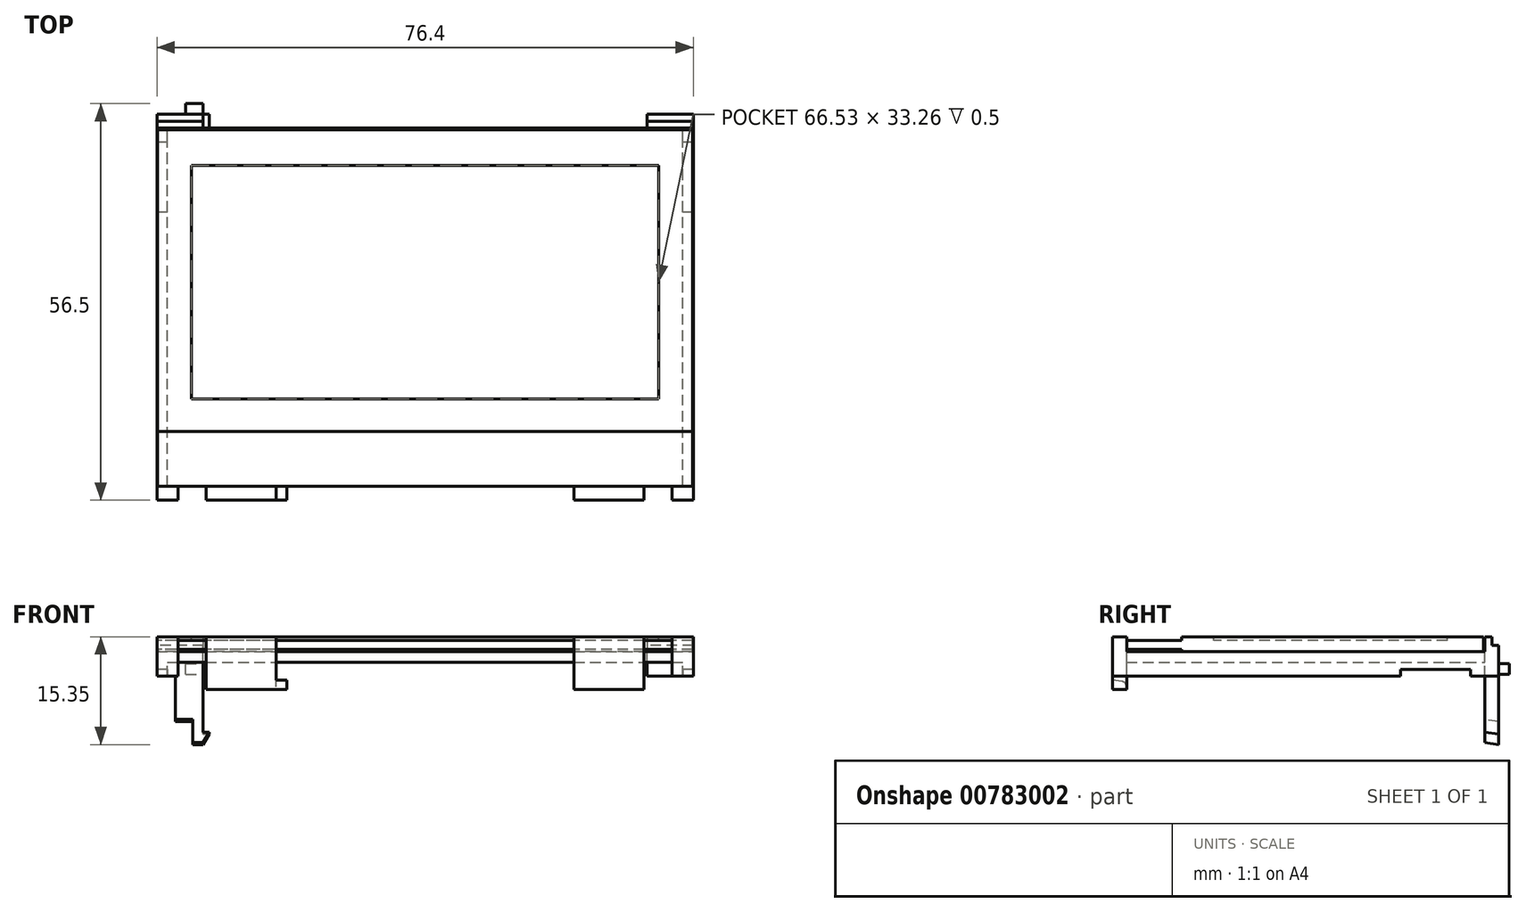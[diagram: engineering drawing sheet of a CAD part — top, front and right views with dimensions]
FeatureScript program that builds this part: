
annotation { "Feature Type Name" : "Feature", "Feature Type Description" : "" }
export const myFeature = defineFeature(function(context is Context, id is Id, definition is map)
    precondition{}
    {
        {
            var Q0;
            Q0=qCreatedBy(makeId("Top.planeOp"),FACE);
            var sketch = newSketch(context, id + "F0", { "sketchPlane" : qUnion([Q0])});
            skLineSegment(sketch, "E0.bottom", {"start": v(-38.2, 51) * mm, "end": v(38.2, 51) * mm});
            skLineSegment(sketch, "E0.top", {"start": v(-38.2, 0) * mm, "end": v(38.2, 0) * mm});
            skLineSegment(sketch, "E0.left", {"start": v(-38.2, 51) * mm, "end": v(-38.2, 0) * mm});
            skLineSegment(sketch, "E0.right", {"start": v(38.2, 51) * mm, "end": v(38.2, 0) * mm});
            skLineSegment(sketch, "E1", {"start": v(-38.2, 0) * mm, "end": v(-38.2, -2) * mm});
            skLineSegment(sketch, "E2", {"start": v(-38.2, -2) * mm, "end": v(-35.2, -2) * mm});
            skLineSegment(sketch, "E3", {"start": v(-35.2, -2) * mm, "end": v(-31.2, -2) * mm, "construction": true});
            skLineSegment(sketch, "E4", {"start": v(-31.2, -2) * mm, "end": v(-21.2, -2) * mm});
            skLineSegment(sketch, "E5", {"start": v(-21.2, -2) * mm, "end": v(-21.2, 0) * mm});
            skLineSegment(sketch, "E6", {"start": v(-35.2, -2) * mm, "end": v(-35.2, 0) * mm});
            skLineSegment(sketch, "E7", {"start": v(-31.2, -2) * mm, "end": v(-31.2, 0) * mm});
            skLineSegment(sketch, "E8", {"start": v(-38.2, 51) * mm, "end": v(-38.2, 53) * mm});
            skLineSegment(sketch, "E9", {"start": v(-38.2, 53) * mm, "end": v(-31.6, 53) * mm});
            skLineSegment(sketch, "E10", {"start": v(-31.6, 53) * mm, "end": v(-31.6, 51) * mm});
            skLineSegment(sketch, "E11", {"start": v(-36.7, 0) * mm, "end": v(-36.7, 51) * mm});
            skLineSegment(sketch, "E12", {"start": v(0, 0) * mm, "end": v(0, 51) * mm, "construction": true});
            skLineSegment(sketch, "E13.MirrorCS", {"start": v(31.6, 53) * mm, "end": v(31.6, 51) * mm});
            skLineSegment(sketch, "E14.MirrorCS", {"start": v(38.2, 53) * mm, "end": v(31.6, 53) * mm});
            skLineSegment(sketch, "E15.MirrorCS", {"start": v(38.2, 51) * mm, "end": v(38.2, 53) * mm});
            skLineSegment(sketch, "E16.MirrorCS", {"start": v(36.7, 0) * mm, "end": v(36.7, 51) * mm});
            skLineSegment(sketch, "E17.MirrorCS", {"start": v(38.2, 0) * mm, "end": v(38.2, -2) * mm});
            skLineSegment(sketch, "E18.MirrorCS", {"start": v(38.2, -2) * mm, "end": v(35.2, -2) * mm});
            skLineSegment(sketch, "E19.MirrorCS", {"start": v(35.2, -2) * mm, "end": v(35.2, 0) * mm});
            skLineSegment(sketch, "E20.MirrorCS", {"start": v(35.2, -2) * mm, "end": v(31.2, -2) * mm, "construction": true});
            skLineSegment(sketch, "E21.MirrorCS", {"start": v(31.2, -2) * mm, "end": v(31.2, 0) * mm});
            skLineSegment(sketch, "E22.MirrorCS", {"start": v(31.2, -2) * mm, "end": v(21.2, -2) * mm});
            skLineSegment(sketch, "E23.MirrorCS", {"start": v(21.2, -2) * mm, "end": v(21.2, 0) * mm});
            skLineSegment(sketch, "E24", {"start": v(-10, 0) * mm, "end": v(-10, -2) * mm});
            skLineSegment(sketch, "E25", {"start": v(-10, -2) * mm, "end": v(10, -2) * mm});
            skLineSegment(sketch, "E26", {"start": v(10, -2) * mm, "end": v(10, 0) * mm});
            skLineSegment(sketch, "E27", {"start": v(0, 0) * mm, "end": v(0, -2) * mm, "construction": true});
            skSolve(sketch);
        }
        {
            var Q0;
            {var subQ10=sQuery(id+"F0.wireOp",EDGE,"E11");Q0=makeQuery(id+"F0.imprint","IMPRINT",FACE,{"disambiguationData":[TD([[makeQuery(id+"F0.imprint","IMPRINT",EDGE,{"derivedFrom":subQ10}),-1.0]])]});}
            var Q1;
            {var subQ0=sQuery(id+"F0.wireOp",EDGE,"E0.left");Q1=makeQuery(id+"F0.imprint","IMPRINT",FACE,{"disambiguationData":[TD([[makeQuery(id+"F0.imprint","IMPRINT",EDGE,{"derivedFrom":subQ0}),1.0]])]});}
            var Q2;
            {var subQ0=sQuery(id+"F0.wireOp",EDGE,"E0.right");Q2=makeQuery(id+"F0.imprint","IMPRINT",FACE,{"disambiguationData":[TD([[makeQuery(id+"F0.imprint","IMPRINT",EDGE,{"derivedFrom":subQ0}),-1.0]])]});}
            extrude(context, id + "F1", {"entities" : qUnion([Q0, Q1, Q2]), "oppositeDirection" : true, "depth" : 1.5 * mm, "offsetDistance" : 25 * mm});
        }
        {
            var Q0;
            {var subQ3=sQuery(id+"F0.wireOp",EDGE,"E1");Q0=makeQuery(id+"F0.imprint","IMPRINT",FACE,{"disambiguationData":[TD([[makeQuery(id+"F0.imprint","IMPRINT",EDGE,{"derivedFrom":subQ3}),1.0]])]});}
            var Q1;
            {var subQ0=sQuery(id+"F0.wireOp",EDGE,"E17.MirrorCS");Q1=makeQuery(id+"F0.imprint","IMPRINT",FACE,{"disambiguationData":[TD([[makeQuery(id+"F0.imprint","IMPRINT",EDGE,{"derivedFrom":subQ0}),-1.0]])]});}
            var Q2;
            {var subQ0=sQuery(id+"F0.wireOp",EDGE,"E0.right");Q2=makeQuery(id+"F0.imprint","IMPRINT",FACE,{"disambiguationData":[TD([[makeQuery(id+"F0.imprint","IMPRINT",EDGE,{"derivedFrom":subQ0}),-1.0]])]});}
            var Q3;
            {var subQ0=sQuery(id+"F0.wireOp",EDGE,"E13.MirrorCS");Q3=makeQuery(id+"F0.imprint","IMPRINT",FACE,{"disambiguationData":[TD([[makeQuery(id+"F0.imprint","IMPRINT",EDGE,{"derivedFrom":subQ0}),1.0]])]});}
            var Q4;
            {var subQ3=sQuery(id+"F0.wireOp",EDGE,"E8");Q4=makeQuery(id+"F0.imprint","IMPRINT",FACE,{"disambiguationData":[TD([[makeQuery(id+"F0.imprint","IMPRINT",EDGE,{"derivedFrom":subQ3}),-1.0]])]});}
            var Q5;
            {var subQ0=sQuery(id+"F0.wireOp",EDGE,"E0.left");Q5=makeQuery(id+"F0.imprint","IMPRINT",FACE,{"disambiguationData":[TD([[makeQuery(id+"F0.imprint","IMPRINT",EDGE,{"derivedFrom":subQ0}),1.0]])]});}
            extrude(context, id + "F2", {"entities" : qUnion([Q0, Q1, Q2, Q3, Q4, Q5]), "operationType" : NewBodyOperationType.ADD, "oppositeDirection" : true, "depth" : 3.5 * mm, "offsetDistance" : 25 * mm});
        }
        {
            var Q0;
            Q0=makeQuery(id+"F0.imprint","IMPRINT",FACE,{"disambiguationData":[TD([[makeQuery(id+"F0.imprint","IMPRINT",EDGE,{"derivedFrom":sQuery(id+"F0.wireOp",EDGE,"E4")}),1.0]])]});
            var Q1;
            {var subQ0=sQuery(id+"F0.wireOp",EDGE,"E24");Q1=makeQuery(id+"F0.imprint","IMPRINT",FACE,{"disambiguationData":[TD([[makeQuery(id+"F0.imprint","IMPRINT",EDGE,{"derivedFrom":subQ0}),1.0]])]});}
            var Q2;
            {var subQ0=sQuery(id+"F0.wireOp",EDGE,"E21.MirrorCS");Q2=makeQuery(id+"F0.imprint","IMPRINT",FACE,{"disambiguationData":[TD([[makeQuery(id+"F0.imprint","IMPRINT",EDGE,{"derivedFrom":subQ0}),1.0]])]});}
            extrude(context, id + "F3", {"entities" : qUnion([Q0, Q1, Q2]), "operationType" : NewBodyOperationType.ADD, "oppositeDirection" : true, "depth" : 5.4 * mm, "offsetDistance" : 25 * mm});
        }
        {
            var Q0;
            {var subQ3=sQuery(id+"F0.wireOp",EDGE,"E8");Q0=makeQuery(id+"F0.imprint","IMPRINT",FACE,{"disambiguationData":[TD([[makeQuery(id+"F0.imprint","IMPRINT",EDGE,{"derivedFrom":subQ3}),-1.0]])]});}
            var Q1;
            {var subQ0=sQuery(id+"F0.wireOp",EDGE,"E13.MirrorCS");Q1=makeQuery(id+"F0.imprint","IMPRINT",FACE,{"disambiguationData":[TD([[makeQuery(id+"F0.imprint","IMPRINT",EDGE,{"derivedFrom":subQ0}),1.0]])]});}
            var Q2;
            {var subQ3=sQuery(id+"F0.wireOp",EDGE,"E1");Q2=makeQuery(id+"F0.imprint","IMPRINT",FACE,{"disambiguationData":[TD([[makeQuery(id+"F0.imprint","IMPRINT",EDGE,{"derivedFrom":subQ3}),1.0]])]});}
            var Q3;
            Q3=makeQuery(id+"F0.imprint","IMPRINT",FACE,{"disambiguationData":[TD([[makeQuery(id+"F0.imprint","IMPRINT",EDGE,{"derivedFrom":sQuery(id+"F0.wireOp",EDGE,"E4")}),1.0]])]});
            var Q4;
            {var subQ0=sQuery(id+"F0.wireOp",EDGE,"E21.MirrorCS");Q4=makeQuery(id+"F0.imprint","IMPRINT",FACE,{"disambiguationData":[TD([[makeQuery(id+"F0.imprint","IMPRINT",EDGE,{"derivedFrom":subQ0}),1.0]])]});}
            var Q5;
            {var subQ0=sQuery(id+"F0.wireOp",EDGE,"E17.MirrorCS");Q5=makeQuery(id+"F0.imprint","IMPRINT",FACE,{"disambiguationData":[TD([[makeQuery(id+"F0.imprint","IMPRINT",EDGE,{"derivedFrom":subQ0}),-1.0]])]});}
            var Q6;
            {var subQ0=sQuery(id+"F0.wireOp",EDGE,"E24");Q6=makeQuery(id+"F0.imprint","IMPRINT",FACE,{"disambiguationData":[TD([[makeQuery(id+"F0.imprint","IMPRINT",EDGE,{"derivedFrom":subQ0}),1.0]])]});}
            extrude(context, id + "F4", {"entities" : qUnion([Q0, Q1, Q2, Q3, Q4, Q5, Q6]), "operationType" : NewBodyOperationType.ADD, "depth" : 2.1 * mm, "offsetDistance" : 25 * mm});
        }
        {
            var Q0;
            Q0=makeQuery(id+"F1.opExtrude","CAP_FACE",FACE,{"disambiguationData":[OSD([sQuery(id+"F0.wireOp",EDGE,"E0.bottom"),sQuery(id+"F0.wireOp",EDGE,"E0.top"),sQuery(id+"F0.wireOp",EDGE,"E0.left"),sQuery(id+"F0.wireOp",EDGE,"E0.right")])],"isStart":false});
            var sketch = newSketch(context, id + "F5", { "sketchPlane" : qUnion([Q0])});
            skLineSegment(sketch, "E28.bottom", {"start": v(-36, 0) * mm, "end": v(36, 0) * mm});
            skLineSegment(sketch, "E28.top", {"start": v(-36, -30) * mm, "end": v(36, -30) * mm});
            skLineSegment(sketch, "E28.left", {"start": v(-36, 0) * mm, "end": v(-36, -30) * mm});
            skLineSegment(sketch, "E28.right", {"start": v(36, 0) * mm, "end": v(36, -30) * mm});
            skSolve(sketch);
        }
        {
            var Q0;
            Q0 = qSketchRegion(id + "F5", true);
            extrude(context, id + "F6", {"entities" : qUnion([Q0]), "operationType" : NewBodyOperationType.ADD, "depth" : 1 * mm, "offsetDistance" : 25 * mm});
        }
        {
            var Q0;
            Q0=qCreatedBy(makeId("Right.planeOp"),FACE);
            var sketch = newSketch(context, id + "F7", { "sketchPlane" : qUnion([Q0])});
            skLineSegment(sketch, "E29", {"start": v(50.8, 2.1) * mm, "end": v(50.8, 0) * mm});
            skLineSegment(sketch, "E30", {"start": v(50.8, 0) * mm, "end": v(7.8, 0) * mm});
            skLineSegment(sketch, "E31", {"start": v(7.8, 0) * mm, "end": v(7.8, 0.3) * mm});
            skLineSegment(sketch, "E32", {"start": v(7.8, 0.3) * mm, "end": v(7.8, 1.6) * mm});
            skLineSegment(sketch, "E33", {"start": v(7.8, 1.6) * mm, "end": v(7.8, 2.1) * mm});
            skLineSegment(sketch, "E34", {"start": v(7.8, 2.1) * mm, "end": v(50.8, 2.1) * mm});
            skLineSegment(sketch, "E35", {"start": v(7.8, 0.3) * mm, "end": v(0, 0.3) * mm});
            skLineSegment(sketch, "E36", {"start": v(0, 0.3) * mm, "end": v(0, 1.6) * mm});
            skLineSegment(sketch, "E37", {"start": v(0, 1.6) * mm, "end": v(7.8, 1.6) * mm});
            skLineSegment(sketch, "E38", {"start": v(7.8, 0) * mm, "end": v(0, 0) * mm, "construction": true});
            skLineSegment(sketch, "E39", {"start": v(0, 0) * mm, "end": v(0, 0.3) * mm, "construction": true});
            skSolve(sketch);
        }
        {
            var Q0;
            Q0 = qSketchRegion(id + "F7", true);
            extrude(context, id + "F8", {"entities" : qUnion([Q0]), "endBound" : BoundingType.SYMMETRIC, "depth" : 76.2 * mm, "offsetDistance" : 25 * mm});
        }
        {
            var Q0;
            Q0=makeQuery(id+"F8.opExtrude","SWEPT_FACE",FACE,{"disambiguationData":[OSD([sQuery(id+"F7.wireOp",EDGE,"E34")])]});
            var sketch = newSketch(context, id + "F9", { "sketchPlane" : qUnion([Q0])});
            skLineSegment(sketch, "E40.bottom", {"start": v(-33.26, 45.68) * mm, "end": v(33.26, 45.68) * mm});
            skLineSegment(sketch, "E40.top", {"start": v(-33.26, 12.42) * mm, "end": v(33.27, 12.42) * mm});
            skLineSegment(sketch, "E40.left", {"start": v(-33.27, 45.68) * mm, "end": v(-33.27, 12.42) * mm});
            skLineSegment(sketch, "E40.right", {"start": v(33.26, 45.68) * mm, "end": v(33.26, 12.42) * mm});
            skLineSegment(sketch, "E41", {"start": v(0, 50.8) * mm, "end": v(0, 45.68) * mm, "construction": true});
            skSolve(sketch);
        }
        {
            var Q0;
            Q0 = qSketchRegion(id + "F9", true);
            extrude(context, id + "F10", {"entities" : qUnion([Q0]), "operationType" : NewBodyOperationType.REMOVE, "oppositeDirection" : true, "depth" : 0.5 * mm, "offsetDistance" : 25 * mm});
        }
        {
            var Q0;
            {var subQ0=sQuery(id+"F0.wireOp",EDGE,"E5");Q0=makeQuery(id+"F4.boolean.opBoolean","MERGE",FACE,{"derivedFrom":[makeQuery(id+"F3.opExtrude","SWEPT_FACE",FACE,{"disambiguationData":[OSD([subQ0])]}),makeQuery(id+"F4.opExtrude","SWEPT_FACE",FACE,{"disambiguationData":[OSD([subQ0])]})]});}
            var sketch = newSketch(context, id + "F11", { "sketchPlane" : qUnion([Q0])});
            skLineSegment(sketch, "E42.0", {"start": v(-2, -5.4) * mm, "end": v(0, -5.4) * mm});
            skLineSegment(sketch, "E43", {"start": v(0, -5.4) * mm, "end": v(0, -4.32) * mm});
            skLineSegment(sketch, "E44", {"start": v(0, -4.32) * mm, "end": v(-2, -4.04) * mm});
            skLineSegment(sketch, "E45", {"start": v(-2, -4.04) * mm, "end": v(-2, -5.4) * mm});
            skPoint(sketch, "E46.0", {"position": v(0, -2.5) * mm});
            skLineSegment(sketch, "E47", {"start": v(-1, -4.18) * mm, "end": v(-0.75, -2.4) * mm, "construction": true});
            skLineSegment(sketch, "E48", {"start": v(-0.75, -2.4) * mm, "end": v(0, -2.5) * mm, "construction": true});
            skLineSegment(sketch, "E49.0", {"start": v(53, -3.5) * mm, "end": v(51, -3.5) * mm, "construction": true});
            skLineSegment(sketch, "E50", {"start": v(0, -2.5) * mm, "end": v(51, -9.67) * mm, "construction": true});
            skLineSegment(sketch, "E51", {"start": v(53, -3.5) * mm, "end": v(53, -9.95) * mm, "construction": true});
            skLineSegment(sketch, "E52", {"start": v(53, -9.95) * mm, "end": v(51, -9.67) * mm});
            skLineSegment(sketch, "E53", {"start": v(51, -3.5) * mm, "end": v(51, -9.67) * mm, "construction": true});
            skPoint(sketch, "E54.0", {"position": v(0, -5.4) * mm});
            skPoint(sketch, "E54.1", {"position": v(-2, -5.4) * mm});
            skSolve(sketch);
        }
        {
            var Q0;
            Q0 = qSketchRegion(id + "F11", true);
            extrude(context, id + "F12", {"entities" : qUnion([Q0]), "operationType" : NewBodyOperationType.ADD, "depth" : 1.5 * mm, "offsetDistance" : 25 * mm});
        }
        {
            var Q0;
            Q0=makeQuery(id+"F12.opExtrude","SWEPT_EDGE",EDGE,{"disambiguationData":[OSD([sQuery(id+"F0.wireOp",EDGE,"E0.top"),sQuery(id+"F0.wireOp",EDGE,"E5"),sQuery(id+"F11.wireOp",EDGE,"E43"),sQuery(id+"F11.wireOp",EDGE,"E44")])]});
            fillet(context, id + "F13", {"entities" : qUnion([Q0]), "radius" : 0.8 * mm, "tangentPropagation" : true, "allowEdgeOverflow" : false});
        }
        {
            var Q0;
            {var subQ0=sQuery(id+"F0.wireOp",EDGE,"E9");Q0=makeQuery(id+"F4.boolean.opBoolean","MERGE",FACE,{"derivedFrom":[makeQuery(id+"F2.opExtrude","SWEPT_FACE",FACE,{"disambiguationData":[OSD([subQ0])]}),makeQuery(id+"F4.opExtrude","SWEPT_FACE",FACE,{"disambiguationData":[OSD([subQ0])]})]});}
            var sketch = newSketch(context, id + "F14", { "sketchPlane" : qUnion([Q0])});
            skLineSegment(sketch, "E55.bottom", {"start": v(31.6, -3.5) * mm, "end": v(38.2, -3.5) * mm});
            skLineSegment(sketch, "E55.top", {"start": v(31.6, 2.1) * mm, "end": v(38.2, 2.1) * mm});
            skLineSegment(sketch, "E55.left", {"start": v(31.6, -3.5) * mm, "end": v(31.6, 2.1) * mm});
            skLineSegment(sketch, "E55.right", {"start": v(38.2, -3.5) * mm, "end": v(38.2, 2.1) * mm});
            skLineSegment(sketch, "E56", {"start": v(31.6, -3.5) * mm, "end": v(31.6, -11.75) * mm});
            skLineSegment(sketch, "E57", {"start": v(31.6, -11.75) * mm, "end": v(30.73, -11.75) * mm});
            skLineSegment(sketch, "E58", {"start": v(30.73, -11.75) * mm, "end": v(31.6, -13.25) * mm});
            skLineSegment(sketch, "E59", {"start": v(31.6, -13.25) * mm, "end": v(33.1, -13.25) * mm});
            skLineSegment(sketch, "E60", {"start": v(33.1, -13.25) * mm, "end": v(33.1, -9.95) * mm});
            skLineSegment(sketch, "E61", {"start": v(33.1, -9.95) * mm, "end": v(35.6, -9.95) * mm});
            skLineSegment(sketch, "E62", {"start": v(35.6, -9.95) * mm, "end": v(35.6, -3.5) * mm});
            skLineSegment(sketch, "E63", {"start": v(31.6, -11.75) * mm, "end": v(31.6, -13.25) * mm, "construction": true});
            skPoint(sketch, "E64.0", {"position": v(21.2, -9.95) * mm});
            skLineSegment(sketch, "E65", {"start": v(33.1, -9.95) * mm, "end": v(21.2, -9.95) * mm, "construction": true});
            skSolve(sketch);
        }
        {
            var Q0;
            {var subQ0=sQuery(id+"F14.wireOp",EDGE,"E56");Q0=makeQuery(id+"F14.imprint","IMPRINT",FACE,{"disambiguationData":[TD([[makeQuery(id+"F14.imprint","IMPRINT",EDGE,{"derivedFrom":subQ0}),1.0]])]});}
            var Q1;
            Q1=sQuery(id+"F11.wireOp",EDGE,"E52");
            sweep(context, id + "F15", {"operationType" : NewBodyOperationType.ADD, "profiles" : qUnion([Q0]), "path" : qUnion([Q1])});
        }
        {
            var Q0;
            {var subQ0=sQuery(id+"F0.wireOp",EDGE,"E9");Q0=makeQuery(id+"F15.boolean.opBoolean","MERGE",FACE,{"derivedFrom":[makeQuery(id+"F4.boolean.opBoolean","MERGE",FACE,{"derivedFrom":[makeQuery(id+"F2.opExtrude","SWEPT_FACE",FACE,{"disambiguationData":[OSD([subQ0])]}),makeQuery(id+"F4.opExtrude","SWEPT_FACE",FACE,{"disambiguationData":[OSD([subQ0])]})]}),makeQuery(id+"F15.opSweep","CAP_FACE",FACE,{"disambiguationData":[OSD([sQuery(id+"F11.wireOp",VERTEX,"E52.start"),sQuery(id+"F14.wireOp",EDGE,"E55.bottom"),sQuery(id+"F14.wireOp",EDGE,"E56"),sQuery(id+"F14.wireOp",EDGE,"E57"),sQuery(id+"F14.wireOp",EDGE,"E58"),sQuery(id+"F14.wireOp",EDGE,"E59"),sQuery(id+"F14.wireOp",EDGE,"E60"),sQuery(id+"F14.wireOp",EDGE,"E61"),sQuery(id+"F14.wireOp",EDGE,"E62")])],"isStart":true})]});}
            var sketch = newSketch(context, id + "F16", { "sketchPlane" : qUnion([Q0])});
            skLineSegment(sketch, "E66.bottom", {"start": v(34.1, -3.2) * mm, "end": v(31.6, -3.2) * mm});
            skLineSegment(sketch, "E66.top", {"start": v(34.1, -1.7) * mm, "end": v(31.6, -1.7) * mm});
            skLineSegment(sketch, "E66.left", {"start": v(34.1, -3.2) * mm, "end": v(34.1, -1.7) * mm});
            skLineSegment(sketch, "E66.right", {"start": v(31.6, -3.2) * mm, "end": v(31.6, -1.7) * mm});
            skSolve(sketch);
        }
        {
            var Q0;
            Q0 = qSketchRegion(id + "F16", true);
            extrude(context, id + "F17", {"entities" : qUnion([Q0]), "operationType" : NewBodyOperationType.ADD, "depth" : 1.5 * mm, "offsetDistance" : 25 * mm});
        }
        {
            var Q0;
            {var subQ0=sQuery(id+"F0.wireOp",EDGE,"E8");var subQ1=sQuery(id+"F0.wireOp",EDGE,"E1");var subQ2=sQuery(id+"F0.wireOp",EDGE,"E0.left");Q0=makeQuery(id+"F4.boolean.opBoolean","MERGE",FACE,{"derivedFrom":[makeQuery(id+"F2.boolean.opBoolean","MERGE",FACE,{"derivedFrom":[makeQuery(id+"F1.opExtrude","SWEPT_FACE",FACE,{"disambiguationData":[OSD([subQ2])]}),makeQuery(id+"F2.opExtrude","SWEPT_FACE",FACE,{"disambiguationData":[OSD([subQ2,subQ1,subQ0])]})]}),makeQuery(id+"F4.opExtrude","SWEPT_FACE",FACE,{"disambiguationData":[OSD([subQ1])]}),makeQuery(id+"F4.opExtrude","SWEPT_FACE",FACE,{"disambiguationData":[OSD([subQ0])]})]});}
            var sketch = newSketch(context, id + "F18", { "sketchPlane" : qUnion([Q0])});
            skLineSegment(sketch, "E67.bottom", {"start": v(-49, -3.5) * mm, "end": v(-39, -3.5) * mm});
            skLineSegment(sketch, "E67.top", {"start": v(-49, -2.5) * mm, "end": v(-39, -2.5) * mm});
            skLineSegment(sketch, "E67.left", {"start": v(-49, -3.5) * mm, "end": v(-49, -2.5) * mm});
            skLineSegment(sketch, "E67.right", {"start": v(-39, -3.5) * mm, "end": v(-39, -2.5) * mm});
            skLineSegment(sketch, "E68.bottom", {"start": v(-53, 2.1) * mm, "end": v(-52, 2.1) * mm});
            skLineSegment(sketch, "E68.top", {"start": v(-53, 0.9) * mm, "end": v(-52, 0.9) * mm});
            skLineSegment(sketch, "E68.left", {"start": v(-53, 2.1) * mm, "end": v(-53, 0.9) * mm});
            skLineSegment(sketch, "E68.right", {"start": v(-52, 2.1) * mm, "end": v(-52, 0.9) * mm});
            skPoint(sketch, "E69.0", {"position": v(-51, 0) * mm});
            skSolve(sketch);
        }
        {
            var Q0;
            Q0 = qSketchRegion(id + "F18", true);
            var Q1;
            Q1=makeQuery(id+"F2.opExtrude","SWEPT_FACE",FACE,{"disambiguationData":[OSD([sQuery(id+"F0.wireOp",EDGE,"E11")])]});
            extrude(context, id + "F19", {"entities" : qUnion([Q0]), "operationType" : NewBodyOperationType.REMOVE, "endBound" : BoundingType.THROUGH_ALL, "oppositeDirection" : true, "depth" : 25 * mm, "endBoundEntityFace" : qUnion([Q1]), "offsetDistance" : 25 * mm});
        }
        {
            var Q0;
            Q0=makeQuery(id+"F6.opExtrude","CAP_FACE",FACE,{"disambiguationData":[OSD([sQuery(id+"F5.wireOp",EDGE,"E28.bottom"),sQuery(id+"F5.wireOp",EDGE,"E28.top"),sQuery(id+"F5.wireOp",EDGE,"E28.left"),sQuery(id+"F5.wireOp",EDGE,"E28.right")])],"isStart":false});
            var Q1;
            Q1=makeQuery(id+"F1.opExtrude","CAP_FACE",FACE,{"disambiguationData":[OSD([sQuery(id+"F0.wireOp",EDGE,"E0.bottom"),sQuery(id+"F0.wireOp",EDGE,"E0.top"),sQuery(id+"F0.wireOp",EDGE,"E0.left"),sQuery(id+"F0.wireOp",EDGE,"E0.right")])],"isStart":false});
            extrude(context, id + "F20", {"entities" : qUnion([Q0]), "operationType" : NewBodyOperationType.REMOVE, "endBound" : BoundingType.UP_TO_SURFACE, "oppositeDirection" : true, "depth" : 25 * mm, "endBoundEntityFace" : qUnion([Q1]), "offsetDistance" : 25 * mm});
        }
        {
            var Q0;
            Q0=makeQuery(id+"F3.opExtrude","CAP_FACE",FACE,{"disambiguationData":[OSD([sQuery(id+"F0.wireOp",EDGE,"E0.top"),sQuery(id+"F0.wireOp",EDGE,"E24"),sQuery(id+"F0.wireOp",EDGE,"E25"),sQuery(id+"F0.wireOp",EDGE,"E26")])],"isStart":false});
            extrude(context, id + "F21", {"entities" : qUnion([Q0]), "operationType" : NewBodyOperationType.REMOVE, "endBound" : BoundingType.THROUGH_ALL, "oppositeDirection" : true, "depth" : 25 * mm, "offsetDistance" : 25 * mm});
        }
    });
